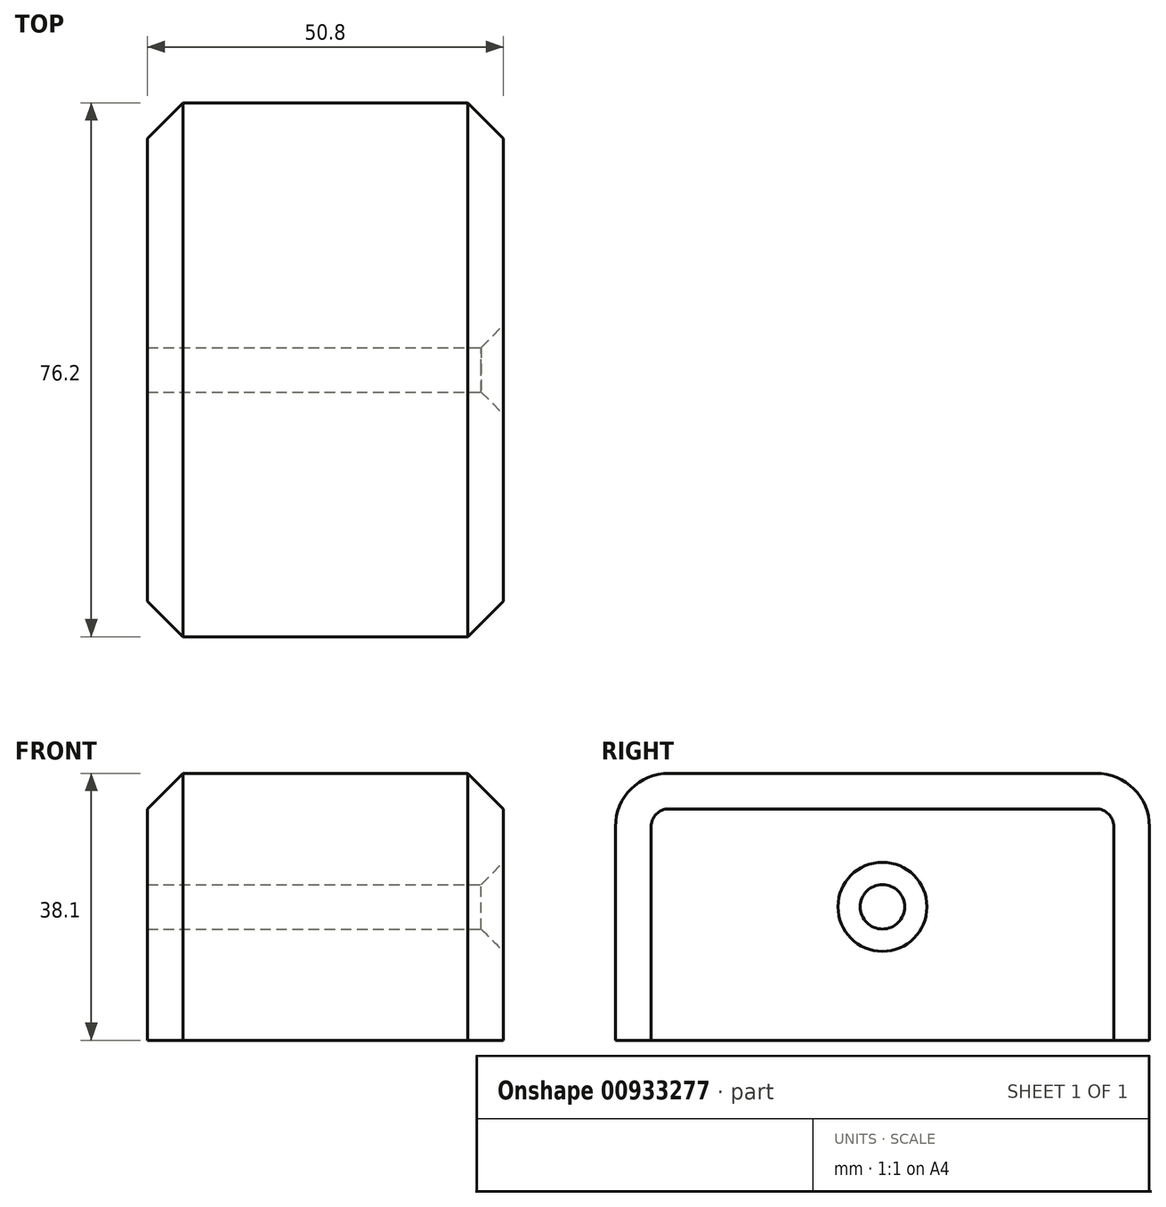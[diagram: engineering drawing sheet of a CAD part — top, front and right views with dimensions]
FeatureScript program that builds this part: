
annotation { "Feature Type Name" : "Feature", "Feature Type Description" : "" }
export const myFeature = defineFeature(function(context is Context, id is Id, definition is map)
    precondition{}
    {
        {
            var Q0;
            Q0=qCreatedBy(makeId("Front.planeOp"),FACE);
            var sketch = newSketch(context, id + "F0", { "sketchPlane" : qUnion([Q0])});
            skLineSegment(sketch, "E0.bottom", {"start": v(0, 0) * mm, "end": v(50.8, 0) * mm});
            skLineSegment(sketch, "E0.top", {"start": v(0, 38.1) * mm, "end": v(50.8, 38.1) * mm});
            skLineSegment(sketch, "E0.left", {"start": v(0, 0) * mm, "end": v(0, 38.1) * mm});
            skLineSegment(sketch, "E0.right", {"start": v(50.8, 0) * mm, "end": v(50.8, 38.1) * mm});
            skSolve(sketch);
        }
        {
            var Q0;
            Q0=makeQuery(id+"F0.imprint","IMPRINT",FACE,{"disambiguationData":[TD([[makeQuery(id+"F0.imprint","IMPRINT",EDGE,{"derivedFrom":sQuery(id+"F0.wireOp",EDGE,"E0.bottom")}),1.0]])]});
            var Q1;
            Q1=sQuery(id+"F0.wireOp",EDGE,"E0.top");
            extrude(context, id + "F1", {"entities" : qUnion([Q0]), "surfaceEntities" : qUnion([Q1]), "depth" : 76.2 * mm, "offsetDistance" : 25.4 * mm});
        }
        {
            var Q0;
            Q0=makeQuery(id+"F1.opExtrude","CAP_EDGE",EDGE,{"disambiguationData":[OSD([sQuery(id+"F0.wireOp",EDGE,"E0.top")])],"isStart":false});
            var Q1;
            Q1=makeQuery(id+"F1.opExtrude","CAP_EDGE",EDGE,{"disambiguationData":[OSD([sQuery(id+"F0.wireOp",EDGE,"E0.top")])],"isStart":true});
            fillet(context, id + "F2", {"entities" : qUnion([Q0, Q1]), "radius" : 7.62 * mm, "tangentPropagation" : true, "allowEdgeOverflow" : false});
        }
        {
            var Q0;
            Q0=makeQuery(id+"F1.opExtrude","SWEPT_EDGE",EDGE,{"disambiguationData":[OSD([sQuery(id+"F0.wireOp",EDGE,"E0.top"),sQuery(id+"F0.wireOp",EDGE,"E0.right")])]});
            var Q1;
            Q1=makeQuery(id+"F1.opExtrude","SWEPT_EDGE",EDGE,{"disambiguationData":[OSD([sQuery(id+"F0.wireOp",EDGE,"E0.top"),sQuery(id+"F0.wireOp",EDGE,"E0.left")])]});
            chamfer(context, id + "F3", {"entities" : qUnion([Q0, Q1]), "width" : 5.08 * mm, "tangentPropagation" : true});
        }
        {
            var Q0;
            Q0=makeQuery(id+"F1.opExtrude","SWEPT_FACE",FACE,{"disambiguationData":[OSD([sQuery(id+"F0.wireOp",EDGE,"E0.right")])]});
            var sketch = newSketch(context, id + "F4", { "sketchPlane" : qUnion([Q0])});
            skPoint(sketch, "E1", {"position": v(-38.1, 19.05) * mm});
            skSolve(sketch);
        }
        {
            var Q0;
            Q0=sQuery(id+"F4.wireOp",VERTEX,"E1");
            var Q1;
            Q1=makeQuery(id+"F1.opExtrude","SWEPT_BODY",BODY,{"disambiguationData":[OSD([sQuery(id+"F0.wireOp",EDGE,"E0.bottom"),sQuery(id+"F0.wireOp",EDGE,"E0.top"),sQuery(id+"F0.wireOp",EDGE,"E0.left"),sQuery(id+"F0.wireOp",EDGE,"E0.right")])]});
            hole(context, id + "F5", {"style" : HoleStyle.C_SINK, "endStyle" : HoleEndStyle.THROUGH, "holeDiameter" : 6.35 * mm, "cSinkDiameter" : 12.7 * mm, "cSinkAngle" : 90 * degree, "majorDiameter" : 6.35 * mm, "isTappedThrough" : true, "tappedDepth" : 12.7 * mm, "tapClearance" : 3, "locations" : qUnion([Q0]), "scope" : qUnion([Q1])});
        }
    });
